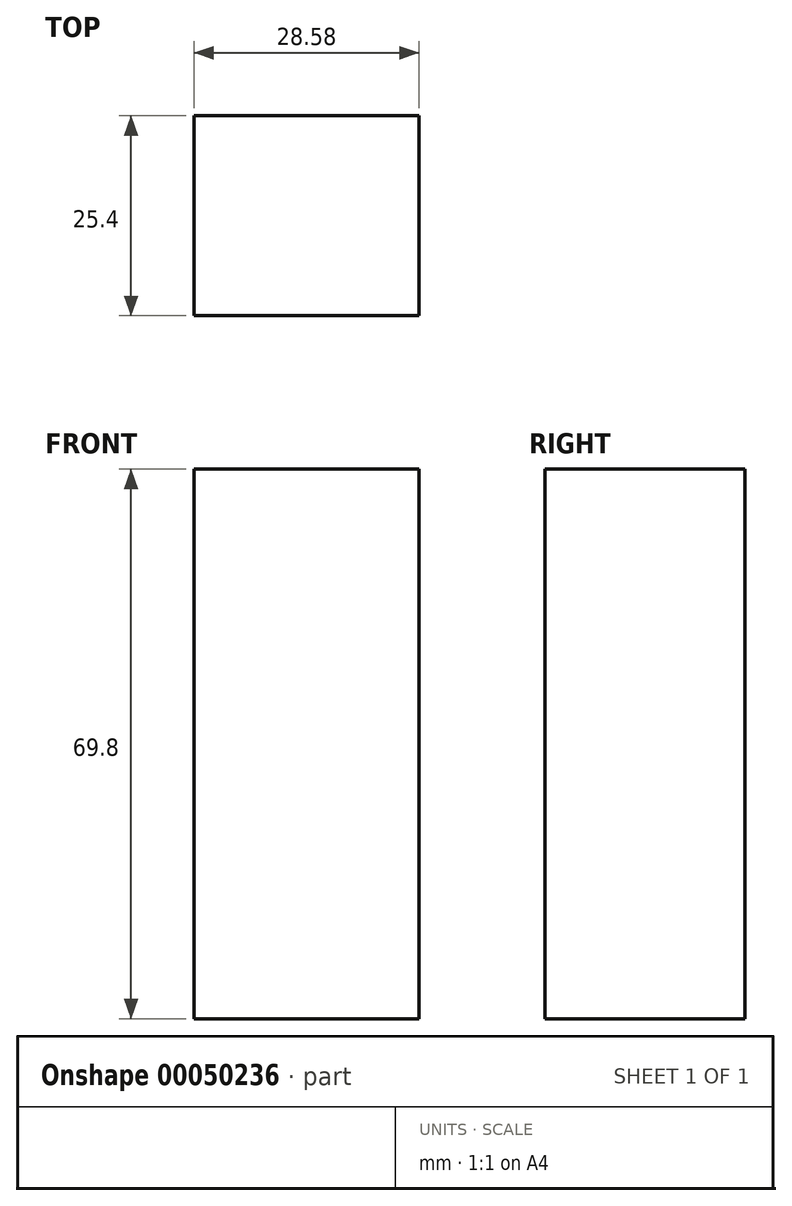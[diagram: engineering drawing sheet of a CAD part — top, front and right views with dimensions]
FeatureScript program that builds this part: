
annotation { "Feature Type Name" : "Feature", "Feature Type Description" : "" }
export const myFeature = defineFeature(function(context is Context, id is Id, definition is map)
    precondition{}
    {
        {
            var Q0;
            Q0=qCreatedBy(makeId("Front.planeOp"),FACE);
            var sketch = newSketch(context, id + "F0", { "sketchPlane" : qUnion([Q0])});
            skLineSegment(sketch, "E0.bottom", {"start": v(-14.58, 14.3) * mm, "end": v(14, 14.3) * mm});
            skLineSegment(sketch, "E0.top", {"start": v(-14.58, -55.51) * mm, "end": v(14, -55.51) * mm});
            skLineSegment(sketch, "E0.left", {"start": v(-14.58, 14.3) * mm, "end": v(-14.58, -55.51) * mm});
            skLineSegment(sketch, "E0.right", {"start": v(14, 14.3) * mm, "end": v(14, -55.51) * mm});
            skSolve(sketch);
        }
        {
            var Q0;
            Q0=makeQuery(id+"F0.imprint","IMPRINT",FACE,{"disambiguationData":[TD([[makeQuery(id+"F0.imprint","IMPRINT",EDGE,{"derivedFrom":sQuery(id+"F0.wireOp",EDGE,"E0.bottom")}),-1.0]])]});
            extrude(context, id + "F1", {"entities" : qUnion([Q0]), "depth" : 25.4 * mm});
        }
    });
